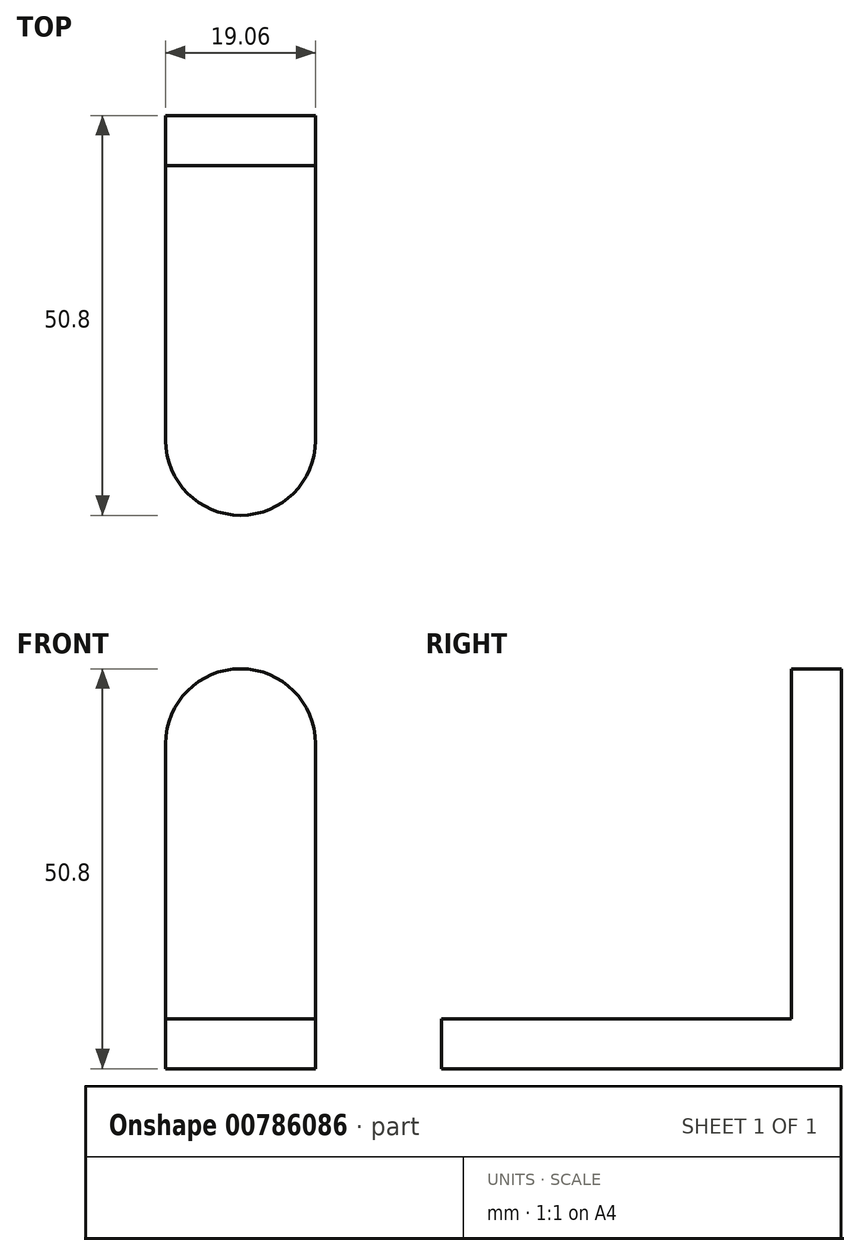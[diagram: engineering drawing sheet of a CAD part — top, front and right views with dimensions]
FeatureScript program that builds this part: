
annotation { "Feature Type Name" : "Feature", "Feature Type Description" : "" }
export const myFeature = defineFeature(function(context is Context, id is Id, definition is map)
    precondition{}
    {
        {
            var Q0;
            Q0=qCreatedBy(makeId("Right.planeOp"),FACE);
            var sketch = newSketch(context, id + "F0", { "sketchPlane" : qUnion([Q0])});
            skLineSegment(sketch, "E0", {"start": v(-50.8, 0) * mm, "end": v(0, 0) * mm});
            skLineSegment(sketch, "E1", {"start": v(0, 0) * mm, "end": v(0, 50.8) * mm});
            skLineSegment(sketch, "E2", {"start": v(0, 50.8) * mm, "end": v(-6.35, 50.8) * mm});
            skLineSegment(sketch, "E3", {"start": v(-6.35, 50.8) * mm, "end": v(-6.35, 6.35) * mm});
            skLineSegment(sketch, "E4", {"start": v(-6.35, 6.35) * mm, "end": v(-50.8, 6.35) * mm});
            skLineSegment(sketch, "E5", {"start": v(-50.8, 6.35) * mm, "end": v(-50.8, 0) * mm});
            skSolve(sketch);
        }
        {
            var Q0;
            Q0 = qSketchRegion(id + "F0", true);
            extrude(context, id + "F1", {"entities" : qUnion([Q0]), "endBound" : BoundingType.SYMMETRIC, "depth" : 19.05 * mm, "offsetDistance" : 25.4 * mm});
        }
        {
            var Q0;
            Q0=makeQuery(id+"F1.opExtrude","CAP_EDGE",EDGE,{"disambiguationData":[OSD([sQuery(id+"F0.wireOp",EDGE,"E2")])],"isStart":false});
            var Q1;
            Q1=makeQuery(id+"F1.opExtrude","CAP_EDGE",EDGE,{"disambiguationData":[OSD([sQuery(id+"F0.wireOp",EDGE,"E2")])],"isStart":true});
            var Q2;
            Q2=makeQuery(id+"F1.opExtrude","CAP_EDGE",EDGE,{"disambiguationData":[OSD([sQuery(id+"F0.wireOp",EDGE,"E5")])],"isStart":false});
            var Q3;
            Q3=makeQuery(id+"F1.opExtrude","CAP_EDGE",EDGE,{"disambiguationData":[OSD([sQuery(id+"F0.wireOp",EDGE,"E5")])],"isStart":true});
            fillet(context, id + "F2", {"entities" : qUnion([Q0, Q1, Q2, Q3]), "radius" : 9.52 * mm, "tangentPropagation" : true, "allowEdgeOverflow" : false});
        }
    });
